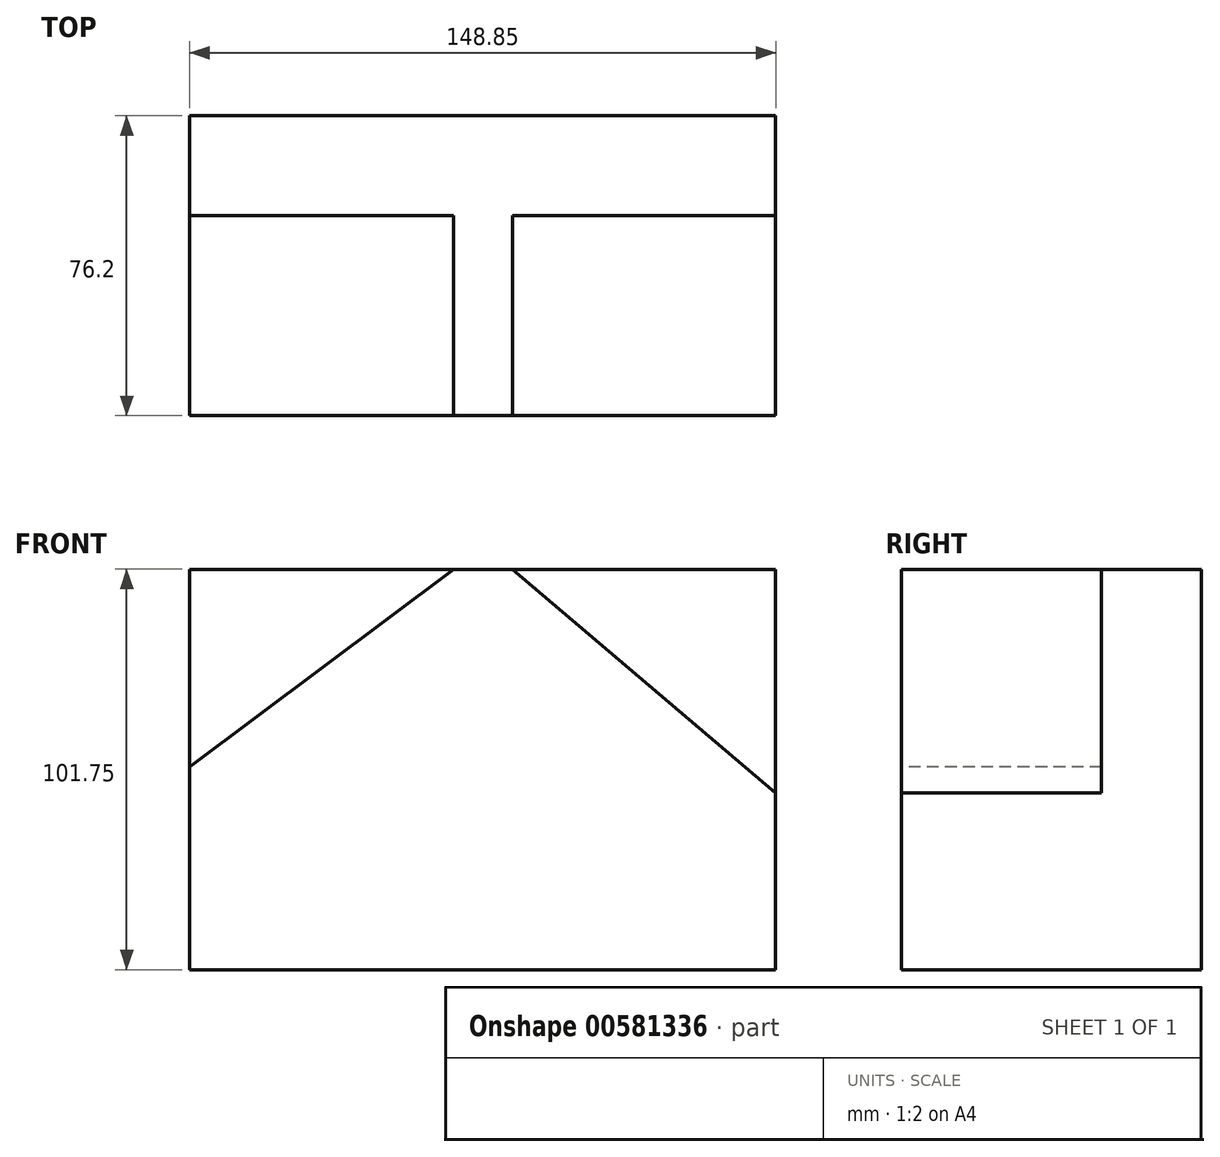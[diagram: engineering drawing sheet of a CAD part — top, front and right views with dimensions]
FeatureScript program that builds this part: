
annotation { "Feature Type Name" : "Feature", "Feature Type Description" : "" }
export const myFeature = defineFeature(function(context is Context, id is Id, definition is map)
    precondition{}
    {
        {
            var Q0;
            Q0=qCreatedBy(makeId("Front.planeOp"),FACE);
            var sketch = newSketch(context, id + "F0", { "sketchPlane" : qUnion([Q0])});
            skLineSegment(sketch, "E0.bottom", {"start": v(-76.12, 76.25) * mm, "end": v(72.73, 76.25) * mm});
            skLineSegment(sketch, "E0.top", {"start": v(-76.12, -25.5) * mm, "end": v(72.73, -25.5) * mm});
            skLineSegment(sketch, "E0.left", {"start": v(-76.12, 76.25) * mm, "end": v(-76.12, -25.5) * mm});
            skLineSegment(sketch, "E0.right", {"start": v(72.73, 76.25) * mm, "end": v(72.73, -25.5) * mm});
            skSolve(sketch);
        }
        {
            var Q0;
            Q0=makeQuery(id+"F0.imprint","IMPRINT",FACE,{"disambiguationData":[TD([[makeQuery(id+"F0.imprint","IMPRINT",EDGE,{"derivedFrom":sQuery(id+"F0.wireOp",EDGE,"E0.bottom")}),-1.0]])]});
            extrude(context, id + "F1", {"entities" : qUnion([Q0]), "depth" : 50.8 * mm, "offsetDistance" : 25.4 * mm});
        }
        {
            var Q0;
            Q0=makeQuery(id+"F1.opExtrude","CAP_FACE",FACE,{"disambiguationData":[OSD([sQuery(id+"F0.wireOp",EDGE,"E0.bottom"),sQuery(id+"F0.wireOp",EDGE,"E0.top"),sQuery(id+"F0.wireOp",EDGE,"E0.left"),sQuery(id+"F0.wireOp",EDGE,"E0.right")])],"isStart":false});
            var sketch = newSketch(context, id + "F2", { "sketchPlane" : qUnion([Q0])});
            skLineSegment(sketch, "E1.bottom", {"start": v(-76.12, 76.25) * mm, "end": v(72.73, 76.25) * mm});
            skLineSegment(sketch, "E1.top", {"start": v(-76.12, -25.5) * mm, "end": v(72.73, -25.5) * mm});
            skLineSegment(sketch, "E1.left", {"start": v(-76.12, 76.25) * mm, "end": v(-76.12, -25.5) * mm});
            skLineSegment(sketch, "E1.right", {"start": v(72.73, 76.25) * mm, "end": v(72.73, -25.5) * mm});
            skLineSegment(sketch, "E2", {"start": v(-9.08, 76.25) * mm, "end": v(-76.12, 26.01) * mm});
            skLineSegment(sketch, "E3", {"start": v(5.9, 76.25) * mm, "end": v(72.73, 19.37) * mm});
            skSolve(sketch);
        }
        {
            var Q0;
            Q0=makeQuery(id+"F2.imprint","IMPRINT",FACE,{"disambiguationData":[TD([[makeQuery(id+"F2.imprint","IMPRINT",EDGE,{"derivedFrom":sQuery(id+"F2.wireOp",EDGE,"E1.bottom")}),-1.0]])]});
            extrude(context, id + "F3", {"entities" : qUnion([Q0]), "operationType" : NewBodyOperationType.REMOVE, "oppositeDirection" : true, "depth" : 25.4 * mm, "offsetDistance" : 25.4 * mm});
        }
        {
            var Q0;
            Q0=makeQuery(id+"F1.opExtrude","CAP_FACE",FACE,{"disambiguationData":[OSD([sQuery(id+"F0.wireOp",EDGE,"E0.bottom"),sQuery(id+"F0.wireOp",EDGE,"E0.top"),sQuery(id+"F0.wireOp",EDGE,"E0.left"),sQuery(id+"F0.wireOp",EDGE,"E0.right")])],"isStart":false});
            var sketch = newSketch(context, id + "F4", { "sketchPlane" : qUnion([Q0])});
            skSolve(sketch);
        }
        {
            var Q0;
            Q0 = qSketchRegion(id + "F4", true);
            var Q1;
            Q1=makeQuery(id+"F1.opExtrude","CAP_FACE",FACE,{"disambiguationData":[OSD([sQuery(id+"F0.wireOp",EDGE,"E0.bottom"),sQuery(id+"F0.wireOp",EDGE,"E0.top"),sQuery(id+"F0.wireOp",EDGE,"E0.left"),sQuery(id+"F0.wireOp",EDGE,"E0.right")])],"isStart":false});
            var Q2;
            Q2=makeQuery(id+"F4.imprint","IMPRINT",FACE,{"disambiguationData":[TD([[makeQuery(id+"F4.imprint","IMPRINT",EDGE,{"derivedFrom":makeQuery(id+"F1.opExtrude","CAP_EDGE",EDGE,{"disambiguationData":[OSD([sQuery(id+"F0.wireOp",EDGE,"E0.top")])],"isStart":false})}),1.0]])]});
            extrude(context, id + "F5", {"entities" : qUnion([Q0, Q1, Q2]), "operationType" : NewBodyOperationType.ADD, "depth" : 25.4 * mm, "offsetDistance" : 25.4 * mm});
        }
    });
